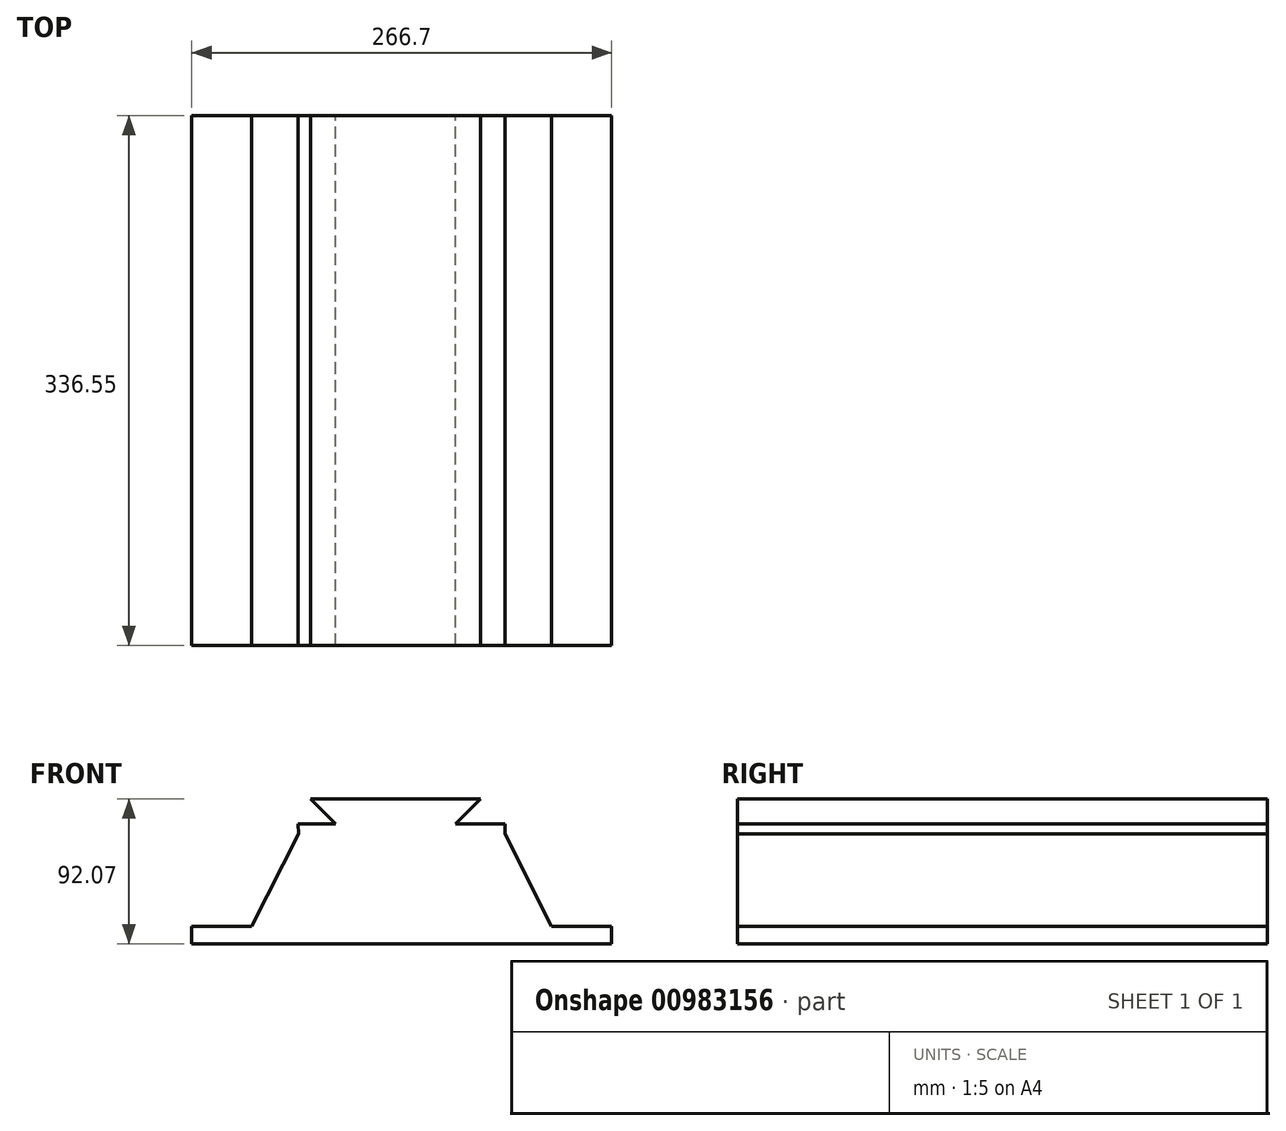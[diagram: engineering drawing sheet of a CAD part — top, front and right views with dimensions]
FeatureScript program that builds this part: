
annotation { "Feature Type Name" : "Feature", "Feature Type Description" : "" }
export const myFeature = defineFeature(function(context is Context, id is Id, definition is map)
    precondition{}
    {
        {
            var Q0;
            Q0=qCreatedBy(makeId("Front.planeOp"),FACE);
            var sketch = newSketch(context, id + "F0", { "sketchPlane" : qUnion([Q0])});
            skLineSegment(sketch, "E0", {"start": v(31.36, -196.26) * mm, "end": v(31.36, -185.15) * mm});
            skLineSegment(sketch, "E1", {"start": v(31.36, -185.15) * mm, "end": v(-6.74, -185.15) * mm});
            skLineSegment(sketch, "E2", {"start": v(-6.74, -185.15) * mm, "end": v(-36.37, -126.41) * mm});
            skLineSegment(sketch, "E3", {"start": v(-36.37, -126.41) * mm, "end": v(-36.29, -120.06) * mm});
            skLineSegment(sketch, "E4", {"start": v(-36.29, -120.06) * mm, "end": v(-67.87, -120.06) * mm});
            skLineSegment(sketch, "E5", {"start": v(-67.87, -120.06) * mm, "end": v(-52, -104.19) * mm});
            skLineSegment(sketch, "E6", {"start": v(-52, -104.19) * mm, "end": v(-159.95, -104.19) * mm});
            skLineSegment(sketch, "E7", {"start": v(-159.95, -104.19) * mm, "end": v(-144.07, -120.06) * mm});
            skLineSegment(sketch, "E8", {"start": v(-144.07, -120.06) * mm, "end": v(-167.94, -120.06) * mm});
            skLineSegment(sketch, "E9", {"start": v(-167.94, -120.06) * mm, "end": v(-167.63, -126.4) * mm});
            skLineSegment(sketch, "E10", {"start": v(-167.63, -126.4) * mm, "end": v(-197.24, -185.15) * mm});
            skLineSegment(sketch, "E11", {"start": v(-197.24, -185.15) * mm, "end": v(-235.34, -185.15) * mm});
            skLineSegment(sketch, "E12", {"start": v(-235.34, -196.26) * mm, "end": v(-235.34, -185.15) * mm});
            skLineSegment(sketch, "E13", {"start": v(-235.34, -196.26) * mm, "end": v(-102, -196.26) * mm});
            skLineSegment(sketch, "E14", {"start": v(-102, -196.26) * mm, "end": v(31.36, -196.26) * mm});
            skSolve(sketch);
        }
        {
            var Q0;
            Q0 = qSketchRegion(id + "F0", true);
            extrude(context, id + "F1", {"entities" : qUnion([Q0]), "depth" : 336.55 * mm, "offsetDistance" : 25.4 * mm});
        }
    });
